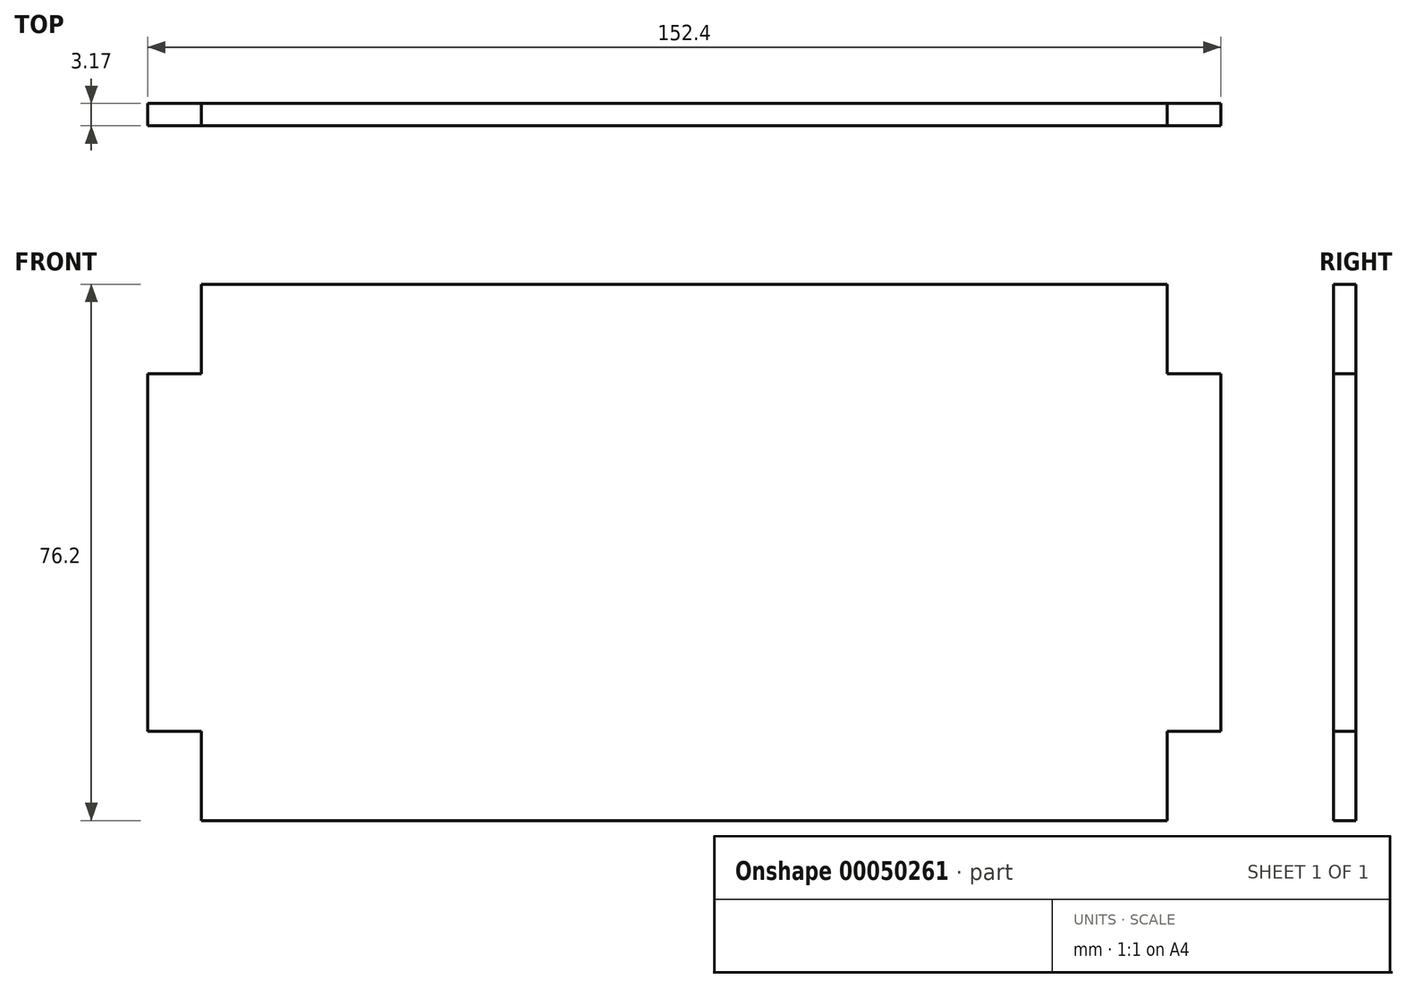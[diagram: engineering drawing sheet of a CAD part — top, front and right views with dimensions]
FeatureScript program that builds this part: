
annotation { "Feature Type Name" : "Feature", "Feature Type Description" : "" }
export const myFeature = defineFeature(function(context is Context, id is Id, definition is map)
    precondition{}
    {
        {
            var Q0;
            Q0=qCreatedBy(makeId("Front.planeOp"),FACE);
            var sketch = newSketch(context, id + "F0", { "sketchPlane" : qUnion([Q0])});
            skLineSegment(sketch, "E0", {"start": v(7.62, 0) * mm, "end": v(144.78, 0) * mm});
            skLineSegment(sketch, "E1", {"start": v(152.4, 12.7) * mm, "end": v(152.4, 63.5) * mm});
            skLineSegment(sketch, "E2", {"start": v(144.78, 76.2) * mm, "end": v(7.62, 76.2) * mm});
            skLineSegment(sketch, "E3", {"start": v(0, 63.5) * mm, "end": v(0, 12.7) * mm});
            skLineSegment(sketch, "E4", {"start": v(7.62, 76.2) * mm, "end": v(7.62, 63.5) * mm});
            skLineSegment(sketch, "E5", {"start": v(7.62, 63.5) * mm, "end": v(0, 63.5) * mm});
            skLineSegment(sketch, "E6", {"start": v(152.4, 63.5) * mm, "end": v(144.78, 63.5) * mm});
            skLineSegment(sketch, "E7", {"start": v(144.78, 63.5) * mm, "end": v(144.78, 76.2) * mm});
            skLineSegment(sketch, "E8", {"start": v(144.78, 0) * mm, "end": v(144.78, 12.7) * mm});
            skLineSegment(sketch, "E9", {"start": v(144.78, 12.7) * mm, "end": v(152.4, 12.7) * mm});
            skLineSegment(sketch, "E10", {"start": v(0, 12.7) * mm, "end": v(7.62, 12.7) * mm});
            skLineSegment(sketch, "E11", {"start": v(7.62, 12.7) * mm, "end": v(7.62, 0) * mm});
            skPoint(sketch, "E12.orphan", {"position": v(0, 76.2) * mm});
            skPoint(sketch, "E13.orphan", {"position": v(0, 0) * mm});
            skSolve(sketch);
        }
        {
            var Q0;
            Q0 = qSketchRegion(id + "F0", true);
            extrude(context, id + "F1", {"entities" : qUnion([Q0]), "depth" : 3.17 * mm});
        }
    });
